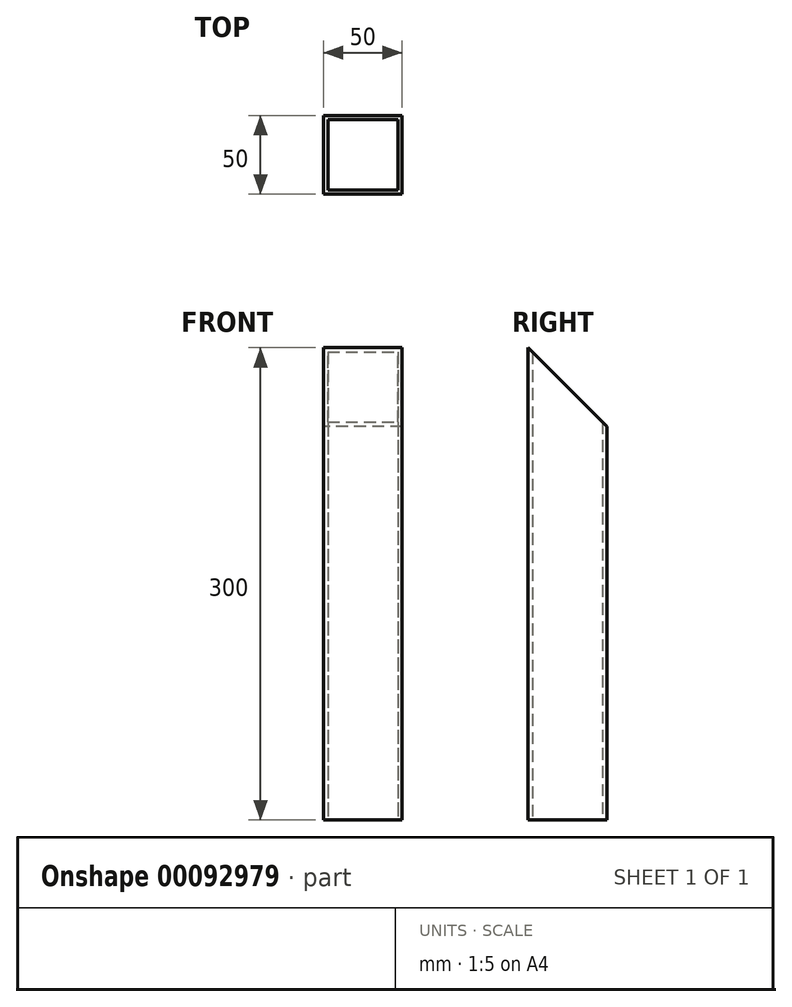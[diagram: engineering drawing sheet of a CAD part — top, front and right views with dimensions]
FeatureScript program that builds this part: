
annotation { "Feature Type Name" : "Feature", "Feature Type Description" : "" }
export const myFeature = defineFeature(function(context is Context, id is Id, definition is map)
    precondition{}
    {
        {
            var Q0;
            Q0=qCreatedBy(makeId("Top.planeOp"),FACE);
            var sketch = newSketch(context, id + "F0", { "sketchPlane" : qUnion([Q0])});
            skLineSegment(sketch, "E0.bottom", {"start": v(-25, 25) * mm, "end": v(25, 25) * mm});
            skLineSegment(sketch, "E0.top", {"start": v(-25, -25) * mm, "end": v(25, -25) * mm});
            skLineSegment(sketch, "E0.left", {"start": v(-25, 25) * mm, "end": v(-25, -25) * mm});
            skLineSegment(sketch, "E0.right", {"start": v(25, 25) * mm, "end": v(25, -25) * mm});
            skPoint(sketch, "E0.middle", {"position": v(0, 0) * mm});
            skLineSegment(sketch, "E1.bottom", {"start": v(-22.25, 22.25) * mm, "end": v(22.25, 22.25) * mm});
            skLineSegment(sketch, "E1.top", {"start": v(-22.25, -22.25) * mm, "end": v(22.25, -22.25) * mm});
            skLineSegment(sketch, "E1.left", {"start": v(-22.25, 22.25) * mm, "end": v(-22.25, -22.25) * mm});
            skLineSegment(sketch, "E1.right", {"start": v(22.25, 22.25) * mm, "end": v(22.25, -22.25) * mm});
            skSolve(sketch);
        }
        {
            var Q0;
            Q0=makeQuery(id+"F0.imprint","IMPRINT",FACE,{"disambiguationData":[TD([[makeQuery(id+"F0.imprint","IMPRINT",EDGE,{"derivedFrom":sQuery(id+"F0.wireOp",EDGE,"E0.bottom")}),-1.0]])]});
            extrude(context, id + "F1", {"entities" : qUnion([Q0]), "depth" : 300 * mm});
        }
        {
            var Q0;
            Q0=qCreatedBy(makeId("Right.planeOp"),FACE);
            var sketch = newSketch(context, id + "F2", { "sketchPlane" : qUnion([Q0])});
            skLineSegment(sketch, "E2", {"start": v(-25, 300) * mm, "end": v(25, 250) * mm});
            skLineSegment(sketch, "E3", {"start": v(25, 250) * mm, "end": v(25, 300) * mm});
            skLineSegment(sketch, "E4", {"start": v(25, 300) * mm, "end": v(-25, 300) * mm});
            skLineSegment(sketch, "E5.0", {"start": v(-25, 300) * mm, "end": v(-25, 0) * mm, "construction": true});
            skLineSegment(sketch, "E6.0", {"start": v(25, 300) * mm, "end": v(-25, 300) * mm, "construction": true});
            skSolve(sketch);
        }
        {
            var Q0;
            Q0 = qSketchRegion(id + "F2", true);
            extrude(context, id + "F3", {"entities" : qUnion([Q0]), "operationType" : NewBodyOperationType.REMOVE, "endBound" : BoundingType.SYMMETRIC, "depth" : 60 * mm});
        }
    });
